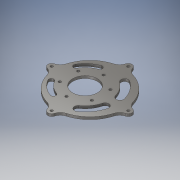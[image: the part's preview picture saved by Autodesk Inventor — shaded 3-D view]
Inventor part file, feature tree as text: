
AUTODESK INVENTOR PART (.ipt)
format: ipt  version: 2019 (Build 230136000, 136)  size: 235,520 bytes
history: native  units: in
note: dims shown in document units (in); Inventor stores cm internally (conversion verified against a paired STEP export)
features: sketch x5, extrude x3, hole x2, projected_geometry x1
ambient origin geometry x8: Origin, YZ Plane, XZ Plane, XY Plane, X Axis, Y Axis, Z Axis, Center Point
bodies: Solid1 (feature_tree)
feature tree (11):
  extrude  "Extrusion1"  Depth=2.5in
  hole  "Hole1"  [1 undecoded]
  hole  "Hole3"  [1 undecoded]
  extrude  "Extrusion3"  Depth=0.5in
  extrude  "Extrusion4"  Depth=1.25in
  sketch  "Sketch1"  dims[d0=2.5in d2=0.75in]
  sketch  "Sketch3"  dims[d3=0.9in d4=0.25in d5=0.0in]
  sketch  "Sketch8"  dims[d10=0.257in d11=0.75in d12=0.438in d13=0.25in d14=0.5635in d15=0.484in d16=0.8108in d20=7.0in]
  sketch  "Sketch9"  dims[d21=0.5in d38=3.75in]
  sketch  "Sketch10"  dims[d39=2.3622in d41=360.0deg d43=0.257in d44=0.75in d45=0.438in d46=0.25in d47=0.5635in d48=1.0in d49=0.8108in d50=1.25in d51=0.75in d52=0.3779in d53=0.3779in d54=0.2749in d55=0.2749in d56=1.0in d57=0.0in d58=4.5in d59=0.5in d60=0.481in d61=30.0deg d62=1.0in d63=0.0in]
  projected_geometry  "Project Cut Edges2"
note: 2 required parameter values undecoded (feature->parameter linkage not recoverable at this tier; creation-order binding heuristic only, values carry confidence <= 0.55)
